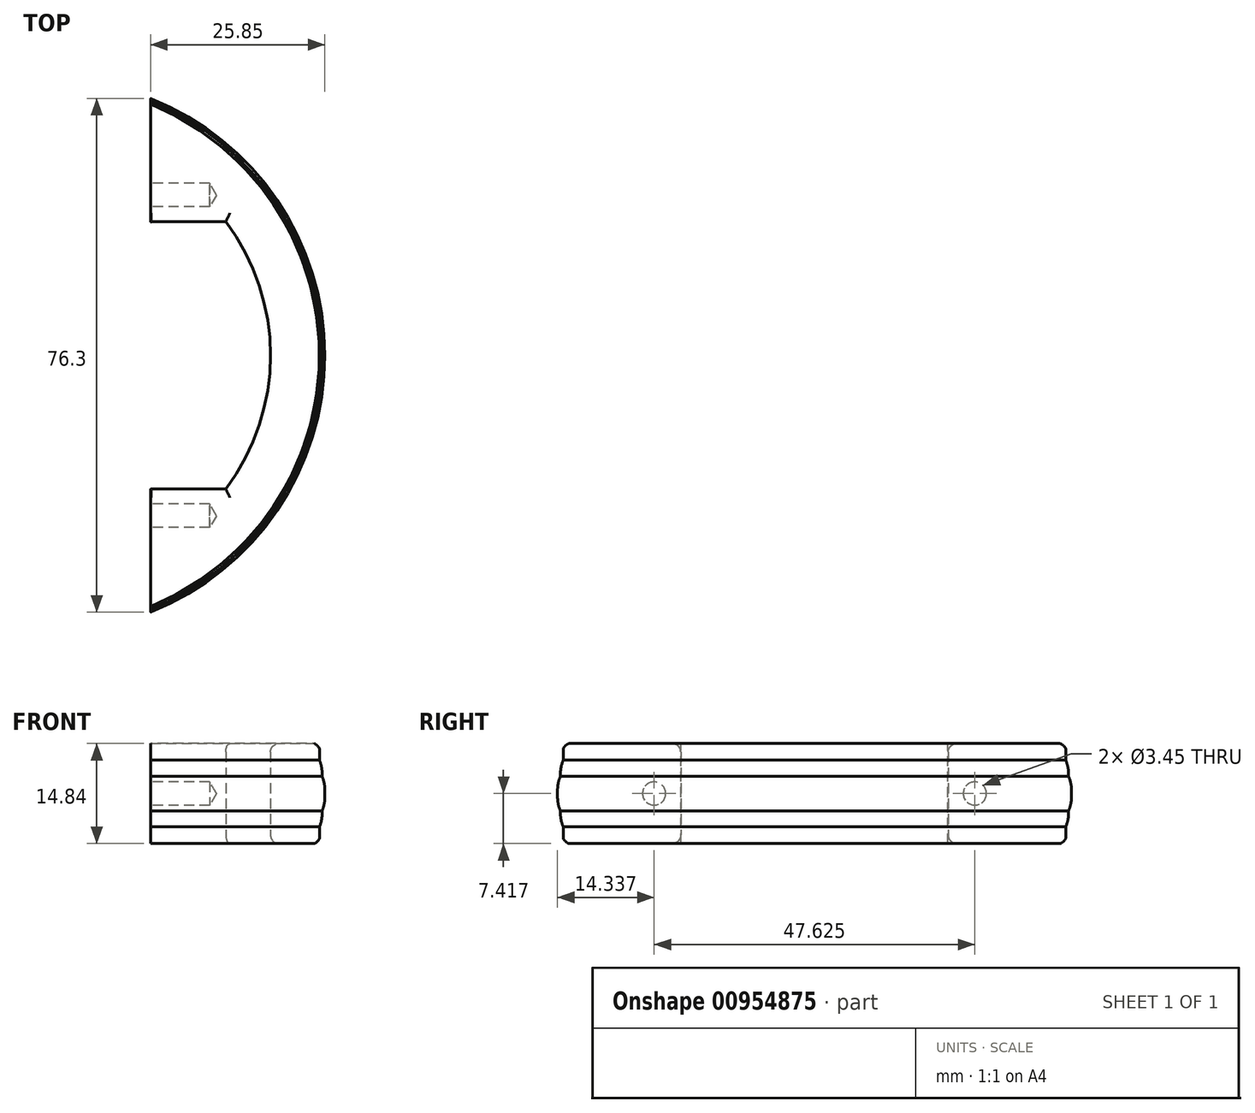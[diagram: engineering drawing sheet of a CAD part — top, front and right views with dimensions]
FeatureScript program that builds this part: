
annotation { "Feature Type Name" : "Feature", "Feature Type Description" : "" }
export const myFeature = defineFeature(function(context is Context, id is Id, definition is map)
    precondition{}
    {
        {
            var Q0;
            Q0=qCreatedBy(makeId("Front.planeOp"),FACE);
            var sketch = newSketch(context, id + "F0", { "sketchPlane" : qUnion([Q0])});
            skLineSegment(sketch, "E0", {"start": v(-55.67, 0) * mm, "end": v(68.03, 0) * mm, "construction": true});
            skLineSegment(sketch, "E1", {"start": v(-7.42, 0) * mm, "end": v(-7.42, 40.28) * mm});
            skLineSegment(sketch, "E2", {"start": v(-7.42, 40.28) * mm, "end": v(-4.96, 40.28) * mm});
            skLineSegment(sketch, "E3", {"start": v(-4.96, 40.28) * mm, "end": v(-4.96, 40.68) * mm});
            skLineSegment(sketch, "E4", {"start": v(-4.96, 40.68) * mm, "end": v(-2.58, 40.68) * mm});
            skLineSegment(sketch, "E5", {"start": v(-2.58, 40.68) * mm, "end": v(-2.58, 41.08) * mm});
            skLineSegment(sketch, "E6", {"start": v(-2.58, 41.08) * mm, "end": v(2.58, 41.08) * mm});
            skLineSegment(sketch, "E7", {"start": v(2.58, 41.08) * mm, "end": v(2.58, 40.68) * mm});
            skLineSegment(sketch, "E8", {"start": v(2.58, 40.68) * mm, "end": v(4.96, 40.68) * mm});
            skLineSegment(sketch, "E9", {"start": v(4.96, 40.68) * mm, "end": v(4.96, 40.28) * mm});
            skLineSegment(sketch, "E10", {"start": v(4.96, 40.28) * mm, "end": v(7.42, 40.28) * mm});
            skLineSegment(sketch, "E11", {"start": v(7.42, 40.28) * mm, "end": v(7.42, 0) * mm});
            skLineSegment(sketch, "E12", {"start": v(7.42, 0) * mm, "end": v(-7.42, 0) * mm});
            skLineSegment(sketch, "E13", {"start": v(0, 0) * mm, "end": v(0, 47.43) * mm, "construction": true});
            skSolve(sketch);
        }
        {
            var Q0;
            Q0=makeQuery(id+"F0.imprint","IMPRINT",FACE,{"disambiguationData":[TD([[makeQuery(id+"F0.imprint","IMPRINT",EDGE,{"derivedFrom":sQuery(id+"F0.wireOp",EDGE,"E1")}),-1.0]])]});
            var Q1;
            Q1=sQuery(id+"F0.wireOp",EDGE,"E0");
            revolve(context, id + "F1", {"surfaceOperationType" : NewSurfaceOperationType.NEW, "entities" : qUnion([Q0]), "axis" : qUnion([Q1]), "revolveType" : RevolveType.FULL});
        }
        {
            var Q0;
            Q0=makeQuery(id+"F1.opRevolve","SWEPT_EDGE",EDGE,{"disambiguationData":[OSD([sQuery(id+"F0.wireOp",EDGE,"E10"),sQuery(id+"F0.wireOp",EDGE,"E11")])]});
            var Q1;
            Q1=makeQuery(id+"F1.opRevolve","SWEPT_EDGE",EDGE,{"disambiguationData":[OSD([sQuery(id+"F0.wireOp",EDGE,"E1"),sQuery(id+"F0.wireOp",EDGE,"E2")])]});
            fillet(context, id + "F2", {"entities" : qUnion([Q0, Q1]), "radius" : 0.76 * mm, "tangentPropagation" : true, "rho" : 0.2, "crossSection" : FilletCrossSection.CONIC, "allowEdgeOverflow" : false});
        }
        {
            var Q0;
            Q0=makeQuery(id+"F1.opRevolve","SWEPT_EDGE",EDGE,{"disambiguationData":[OSD([sQuery(id+"F0.wireOp",EDGE,"E8"),sQuery(id+"F0.wireOp",EDGE,"E9")])]});
            var Q1;
            Q1=makeQuery(id+"F1.opRevolve","SWEPT_EDGE",EDGE,{"disambiguationData":[OSD([sQuery(id+"F0.wireOp",EDGE,"E3"),sQuery(id+"F0.wireOp",EDGE,"E4")])]});
            fillet(context, id + "F3", {"entities" : qUnion([Q0, Q1]), "radius" : 5.08 * mm, "tangentPropagation" : true, "allowEdgeOverflow" : false});
        }
        {
            var Q0;
            Q0=makeQuery(id+"F1.opRevolve","SWEPT_EDGE",EDGE,{"disambiguationData":[OSD([sQuery(id+"F0.wireOp",EDGE,"E6"),sQuery(id+"F0.wireOp",EDGE,"E7")])]});
            var Q1;
            Q1=makeQuery(id+"F1.opRevolve","SWEPT_EDGE",EDGE,{"disambiguationData":[OSD([sQuery(id+"F0.wireOp",EDGE,"E5"),sQuery(id+"F0.wireOp",EDGE,"E6")])]});
            fillet(context, id + "F4", {"entities" : qUnion([Q0, Q1]), "radius" : 5.08 * mm, "tangentPropagation" : true, "allowEdgeOverflow" : false});
        }
        {
            var Q0;
            Q0=qCreatedBy(makeId("Right.planeOp"),FACE);
            var sketch = newSketch(context, id + "F5", { "sketchPlane" : qUnion([Q0])});
            skCircle(sketch, "E14", {"center": v(0, 0) * mm, "radius": 25 * mm});
            skSolve(sketch);
        }
        {
            var Q0;
            Q0=qSketchRegion(id+"F5",true);
            extrude(context, id + "F6", {"entities" : qUnion([Q0]), "operationType" : NewBodyOperationType.REMOVE, "endBound" : BoundingType.THROUGH_ALL, "depth" : 25.4 * mm, "offsetDistance" : 25.4 * mm, "hasSecondDirection" : true, "secondDirectionBound" : SecondDirectionBoundingType.THROUGH_ALL, "secondDirectionOppositeDirection" : true, "secondDirectionDepth" : 25.4 * mm});
        }
        {
            var Q0;
            Q0=qCreatedBy(makeId("Right.planeOp"),FACE);
            var sketch = newSketch(context, id + "F7", { "sketchPlane" : qUnion([Q0])});
            skLineSegment(sketch, "E15", {"start": v(0, 15.23) * mm, "end": v(-38.1, 15.23) * mm, "construction": true});
            skLineSegment(sketch, "E16.MirrorCS", {"start": v(0, 15.23) * mm, "end": v(38.1, 15.23) * mm, "construction": true});
            skLineSegment(sketch, "E17", {"start": v(-59.25, 15.23) * mm, "end": v(65.7, 15.23) * mm});
            skLineSegment(sketch, "E18", {"start": v(65.7, 15.23) * mm, "end": v(65.7, -43.9) * mm});
            skLineSegment(sketch, "E19", {"start": v(65.7, -43.9) * mm, "end": v(-59.25, -43.9) * mm});
            skLineSegment(sketch, "E20", {"start": v(-59.25, -43.9) * mm, "end": v(-59.25, 15.23) * mm});
            skSolve(sketch);
        }
        {
            var Q0;
            Q0=qSketchRegion(id+"F7",true);
            extrude(context, id + "F8", {"entities" : qUnion([Q0]), "operationType" : NewBodyOperationType.REMOVE, "endBound" : BoundingType.THROUGH_ALL, "oppositeDirection" : true, "depth" : 25.4 * mm, "offsetDistance" : 25.4 * mm, "hasSecondDirection" : true, "secondDirectionBound" : SecondDirectionBoundingType.THROUGH_ALL, "secondDirectionOppositeDirection" : false, "secondDirectionDepth" : 25.4 * mm});
        }
        {
            var Q0;
            Q0=qCreatedBy(makeId("Right.planeOp"),FACE);
            var sketch = newSketch(context, id + "F9", { "sketchPlane" : qUnion([Q0])});
            skLineSegment(sketch, "E21", {"start": v(-19.86, 15.26) * mm, "end": v(-19.86, 26.38) * mm});
            skLineSegment(sketch, "E22.MirrorCS", {"start": v(19.86, 15.26) * mm, "end": v(19.86, 26.38) * mm});
            skArc(sketch, "E23", {"start": v(-19.86, 26.38) * mm, "mid": v(0, 33.01) * mm, "end": v(19.86, 26.38) * mm});
            skLineSegment(sketch, "E24", {"start": v(-19.86, 15.26) * mm, "end": v(19.86, 15.26) * mm});
            skSolve(sketch);
        }
        {
            var Q0;
            Q0=qSketchRegion(id+"F9",true);
            extrude(context, id + "F10", {"entities" : qUnion([Q0]), "operationType" : NewBodyOperationType.REMOVE, "endBound" : BoundingType.THROUGH_ALL, "oppositeDirection" : true, "depth" : 25.4 * mm, "offsetDistance" : 25.4 * mm, "hasSecondDirection" : true, "secondDirectionBound" : SecondDirectionBoundingType.THROUGH_ALL, "secondDirectionOppositeDirection" : false, "secondDirectionDepth" : 25.4 * mm});
        }
        {
            var Q0;
            Q0=makeQuery(id+"F10.boolean.opBoolean","INTERSECT",EDGE,{"derivedFrom":[makeQuery(id+"F1.opRevolve","SWEPT_FACE",FACE,{"disambiguationData":[OSD([sQuery(id+"F0.wireOp",EDGE,"E11")])]}),makeQuery(id+"F10.opExtrude","SWEPT_FACE",FACE,{"disambiguationData":[OSD([sQuery(id+"F9.wireOp",EDGE,"E23")])]})]});
            var Q1;
            Q1=makeQuery(id+"F10.boolean.opBoolean","INTERSECT",EDGE,{"derivedFrom":[makeQuery(id+"F1.opRevolve","SWEPT_FACE",FACE,{"disambiguationData":[OSD([sQuery(id+"F0.wireOp",EDGE,"E11")])]}),makeQuery(id+"F10.opExtrude","SWEPT_FACE",FACE,{"disambiguationData":[OSD([sQuery(id+"F9.wireOp",EDGE,"E21")])]})]});
            var Q2;
            Q2=makeQuery(id+"F10.boolean.opBoolean","INTERSECT",EDGE,{"derivedFrom":[makeQuery(id+"F1.opRevolve","SWEPT_FACE",FACE,{"disambiguationData":[OSD([sQuery(id+"F0.wireOp",EDGE,"E11")])]}),makeQuery(id+"F10.opExtrude","SWEPT_FACE",FACE,{"disambiguationData":[OSD([sQuery(id+"F9.wireOp",EDGE,"E22.MirrorCS")])]})]});
            var Q3;
            Q3=makeQuery(id+"F10.boolean.opBoolean","INTERSECT",EDGE,{"derivedFrom":[makeQuery(id+"F1.opRevolve","SWEPT_FACE",FACE,{"disambiguationData":[OSD([sQuery(id+"F0.wireOp",EDGE,"E1")])]}),makeQuery(id+"F10.opExtrude","SWEPT_FACE",FACE,{"disambiguationData":[OSD([sQuery(id+"F9.wireOp",EDGE,"E23")])]})]});
            var Q4;
            Q4=makeQuery(id+"F10.boolean.opBoolean","INTERSECT",EDGE,{"derivedFrom":[makeQuery(id+"F1.opRevolve","SWEPT_FACE",FACE,{"disambiguationData":[OSD([sQuery(id+"F0.wireOp",EDGE,"E1")])]}),makeQuery(id+"F10.opExtrude","SWEPT_FACE",FACE,{"disambiguationData":[OSD([sQuery(id+"F9.wireOp",EDGE,"E21")])]})]});
            var Q5;
            Q5=makeQuery(id+"F10.boolean.opBoolean","INTERSECT",EDGE,{"derivedFrom":[makeQuery(id+"F1.opRevolve","SWEPT_FACE",FACE,{"disambiguationData":[OSD([sQuery(id+"F0.wireOp",EDGE,"E1")])]}),makeQuery(id+"F10.opExtrude","SWEPT_FACE",FACE,{"disambiguationData":[OSD([sQuery(id+"F9.wireOp",EDGE,"E22.MirrorCS")])]})]});
            fillet(context, id + "F11", {"entities" : qUnion([Q0, Q1, Q2, Q3, Q4, Q5]), "radius" : 1.27 * mm, "tangentPropagation" : true, "allowEdgeOverflow" : false});
        }
        {
            var Q0;
            Q0=qCreatedBy(makeId("Top.planeOp"),FACE);
            var sketch = newSketch(context, id + "F12", { "sketchPlane" : qUnion([Q0])});
            skLineSegment(sketch, "E25", {"start": v(-14.34, 23.81) * mm, "end": v(15.86, 23.81) * mm, "construction": true});
            skLineSegment(sketch, "E26.MirrorCS", {"start": v(-14.34, -23.81) * mm, "end": v(15.86, -23.81) * mm, "construction": true});
            skPoint(sketch, "E27", {"position": v(0, 23.81) * mm});
            skPoint(sketch, "E28", {"position": v(0, -23.81) * mm});
            skSolve(sketch);
        }
        {
            var Q0;
            Q0=sQuery(id+"F12.wireOp",VERTEX,"E28");
            var Q1;
            Q1=sQuery(id+"F12.wireOp",VERTEX,"E27");
            var Q2;
            Q2=makeQuery(id+"F1.opRevolve","SWEPT_BODY",BODY,{"disambiguationData":[OSD([sQuery(id+"F0.wireOp",EDGE,"E1"),sQuery(id+"F0.wireOp",EDGE,"E2"),sQuery(id+"F0.wireOp",EDGE,"E3"),sQuery(id+"F0.wireOp",EDGE,"E4"),sQuery(id+"F0.wireOp",EDGE,"E5"),sQuery(id+"F0.wireOp",EDGE,"E6"),sQuery(id+"F0.wireOp",EDGE,"E7"),sQuery(id+"F0.wireOp",EDGE,"E8"),sQuery(id+"F0.wireOp",EDGE,"E9"),sQuery(id+"F0.wireOp",EDGE,"E10"),sQuery(id+"F0.wireOp",EDGE,"E11"),sQuery(id+"F0.wireOp",EDGE,"E12")])]});
            hole(context, id + "F13", {"style" : HoleStyle.SIMPLE, "endStyle" : HoleEndStyle.BLIND, "oppositeDirection" : true, "standardTappedOrClearance" : lookupTablePath({ "standard" : "ANSI", "engagement" : "75%", "pitch" : "32 tpi", "size" : "#8", "type" : "Tapped" }), "standardBlindInLast" : lookupTablePath({ "standard" : "ANSI", "fit" : "Normal", "engagement" : "75%", "pitch" : "32 tpi", "size" : "#8", "type" : "Clearance & tapped" }), "holeDiameter" : 3.45 * mm, "majorDiameter" : 4.17 * mm, "showTappedDepth" : true, "holeDepth" : 23.97 * mm, "isTappedThrough" : true, "tappedDepth" : 21.59 * mm, "tapClearance" : 3, "startFromSketch" : true, "locations" : qUnion([Q0, Q1]), "scope" : qUnion([Q2])});
        }
        {
            var Q0;
            Q0=makeQuery(id+"F1.opRevolve","SWEPT_BODY",BODY,{"disambiguationData":[OSD([sQuery(id+"F0.wireOp",EDGE,"E1"),sQuery(id+"F0.wireOp",EDGE,"E2"),sQuery(id+"F0.wireOp",EDGE,"E3"),sQuery(id+"F0.wireOp",EDGE,"E4"),sQuery(id+"F0.wireOp",EDGE,"E5"),sQuery(id+"F0.wireOp",EDGE,"E6"),sQuery(id+"F0.wireOp",EDGE,"E7"),sQuery(id+"F0.wireOp",EDGE,"E8"),sQuery(id+"F0.wireOp",EDGE,"E9"),sQuery(id+"F0.wireOp",EDGE,"E10"),sQuery(id+"F0.wireOp",EDGE,"E11"),sQuery(id+"F0.wireOp",EDGE,"E12")])]});
            var Q1;
            Q1=makeQuery(id+"F8.boolean.opBoolean","INTERSECT",EDGE,{"disambiguationData":[OD(1.0)],"derivedFrom":[makeQuery(id+"F1.opRevolve","SWEPT_FACE",FACE,{"disambiguationData":[OSD([sQuery(id+"F0.wireOp",EDGE,"E11")])]}),makeQuery(id+"F8.opExtrude","SWEPT_FACE",FACE,{"disambiguationData":[OSD([sQuery(id+"F7.wireOp",EDGE,"E17")])]})]});
            transform(context, id + "F14", {"entities" : qUnion([Q0]), "transformType" : TransformType.ROTATION, "transformAxis" : qUnion([Q1]), "angle" : 90 * degree, "makeCopy" : false});
        }
        {
            var Q0;
            Q0=qCreatedBy(makeId("Right.planeOp"),FACE);
            var sketch = newSketch(context, id + "F15", { "sketchPlane" : qUnion([Q0])});
            skLineSegment(sketch, "E29", {"start": v(-2.35, 15.24) * mm, "end": v(-2.35, 0) * mm});
            skSolve(sketch);
        }
        {
            var Q0;
            Q0=makeQuery(id+"F1.opRevolve","SWEPT_BODY",BODY,{"disambiguationData":[OSD([sQuery(id+"F0.wireOp",EDGE,"E1"),sQuery(id+"F0.wireOp",EDGE,"E2"),sQuery(id+"F0.wireOp",EDGE,"E3"),sQuery(id+"F0.wireOp",EDGE,"E4"),sQuery(id+"F0.wireOp",EDGE,"E5"),sQuery(id+"F0.wireOp",EDGE,"E6"),sQuery(id+"F0.wireOp",EDGE,"E7"),sQuery(id+"F0.wireOp",EDGE,"E8"),sQuery(id+"F0.wireOp",EDGE,"E9"),sQuery(id+"F0.wireOp",EDGE,"E10"),sQuery(id+"F0.wireOp",EDGE,"E11"),sQuery(id+"F0.wireOp",EDGE,"E12")])]});
            var Q1;
            Q1=sQuery(id+"F15.wireOp",EDGE,"E29");
            transform(context, id + "F16", {"entities" : qUnion([Q0]), "transformType" : TransformType.TRANSLATION_ENTITY, "oppositeDirectionEntity" : false, "transformLine" : qUnion([Q1]), "makeCopy" : false});
        }
    });
